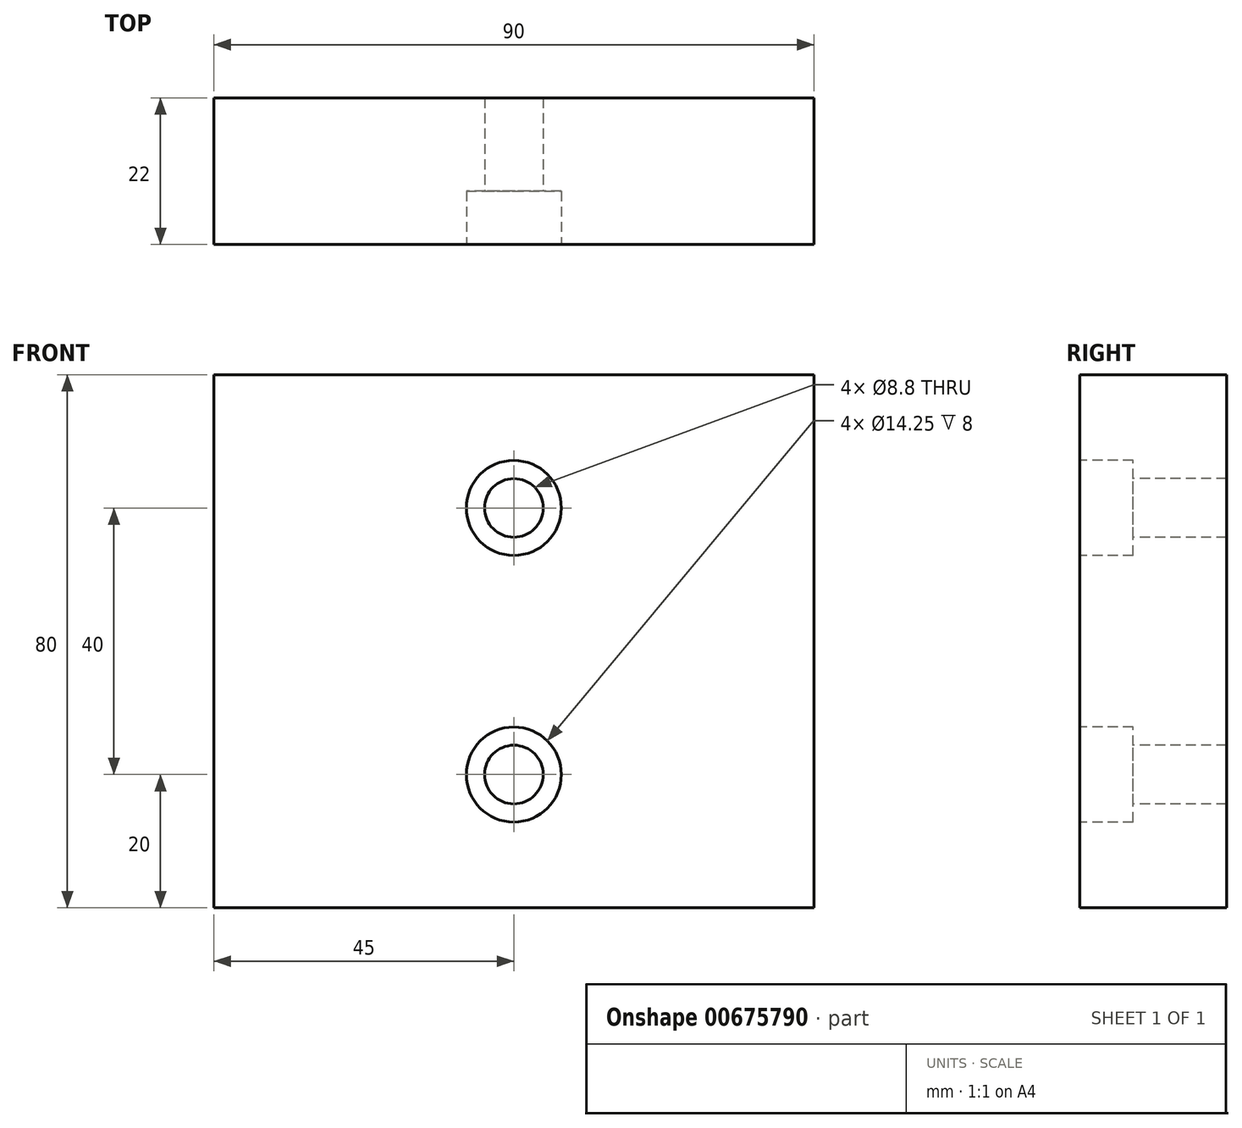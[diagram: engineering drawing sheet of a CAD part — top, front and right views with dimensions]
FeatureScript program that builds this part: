
annotation { "Feature Type Name" : "Feature", "Feature Type Description" : "" }
export const myFeature = defineFeature(function(context is Context, id is Id, definition is map)
    precondition{}
    {
        {
            var Q0;
            Q0=qCreatedBy(makeId("Front.planeOp"),FACE);
            var sketch = newSketch(context, id + "F0", { "sketchPlane" : qUnion([Q0])});
            skLineSegment(sketch, "E0.bottom", {"start": v(45, 40) * mm, "end": v(-45, 40) * mm});
            skLineSegment(sketch, "E0.top", {"start": v(45, -40) * mm, "end": v(-45, -40) * mm});
            skLineSegment(sketch, "E0.left", {"start": v(45, 40) * mm, "end": v(45, -40) * mm});
            skLineSegment(sketch, "E0.right", {"start": v(-45, 40) * mm, "end": v(-45, -40) * mm});
            skPoint(sketch, "E0.middle", {"position": v(0, 0) * mm});
            skSolve(sketch);
        }
        {
            var Q0;
            Q0=makeQuery(id+"F0.imprint","IMPRINT",FACE,{"disambiguationData":[TD([[makeQuery(id+"F0.imprint","IMPRINT",EDGE,{"derivedFrom":sQuery(id+"F0.wireOp",EDGE,"E0.bottom")}),1.0]])]});
            extrude(context, id + "F1", {"entities" : qUnion([Q0]), "depth" : 22 * mm, "offsetDistance" : 25 * mm});
        }
        {
            var Q0;
            Q0=makeQuery(id+"F1.opExtrude","CAP_FACE",FACE,{"disambiguationData":[OSD([sQuery(id+"F0.wireOp",EDGE,"E0.bottom"),sQuery(id+"F0.wireOp",EDGE,"E0.top"),sQuery(id+"F0.wireOp",EDGE,"E0.left"),sQuery(id+"F0.wireOp",EDGE,"E0.right")])],"isStart":false});
            var sketch = newSketch(context, id + "F2", { "sketchPlane" : qUnion([Q0])});
            skPoint(sketch, "E1", {"position": v(0, 20) * mm});
            skPoint(sketch, "E2", {"position": v(0, -20) * mm});
            skSolve(sketch);
        }
        {
            var Q0;
            Q0=sQuery(id+"F2.wireOp",VERTEX,"E1");
            var Q1;
            Q1=sQuery(id+"F2.wireOp",VERTEX,"E2");
            var Q2;
            Q2=makeQuery(id+"F1.opExtrude","SWEPT_BODY",BODY,{"disambiguationData":[OSD([sQuery(id+"F0.wireOp",EDGE,"E0.bottom"),sQuery(id+"F0.wireOp",EDGE,"E0.top"),sQuery(id+"F0.wireOp",EDGE,"E0.left"),sQuery(id+"F0.wireOp",EDGE,"E0.right")])]});
            hole(context, id + "F3", {"style" : HoleStyle.C_BORE, "endStyle" : HoleEndStyle.THROUGH, "standardTappedOrClearance" : lookupTablePath({ "standard" : "ISO", "fit" : "Normal", "size" : "M8", "type" : "Clearance" }), "standardBlindInLast" : lookupTablePath({ "fit" : "Standard", "standard" : "ISO", "size" : "M8", "type" : "Clearance" }), "holeDiameter" : 8.8 * mm, "cBoreDiameter" : 14.25 * mm, "cBoreDepth" : 8 * mm, "majorDiameter" : 8 * mm, "isTappedThrough" : true, "tappedDepth" : 17.25 * mm, "tapClearance" : 3, "startFromSketch" : true, "locations" : qUnion([Q0, Q1]), "scope" : qUnion([Q2])});
        }
    });
